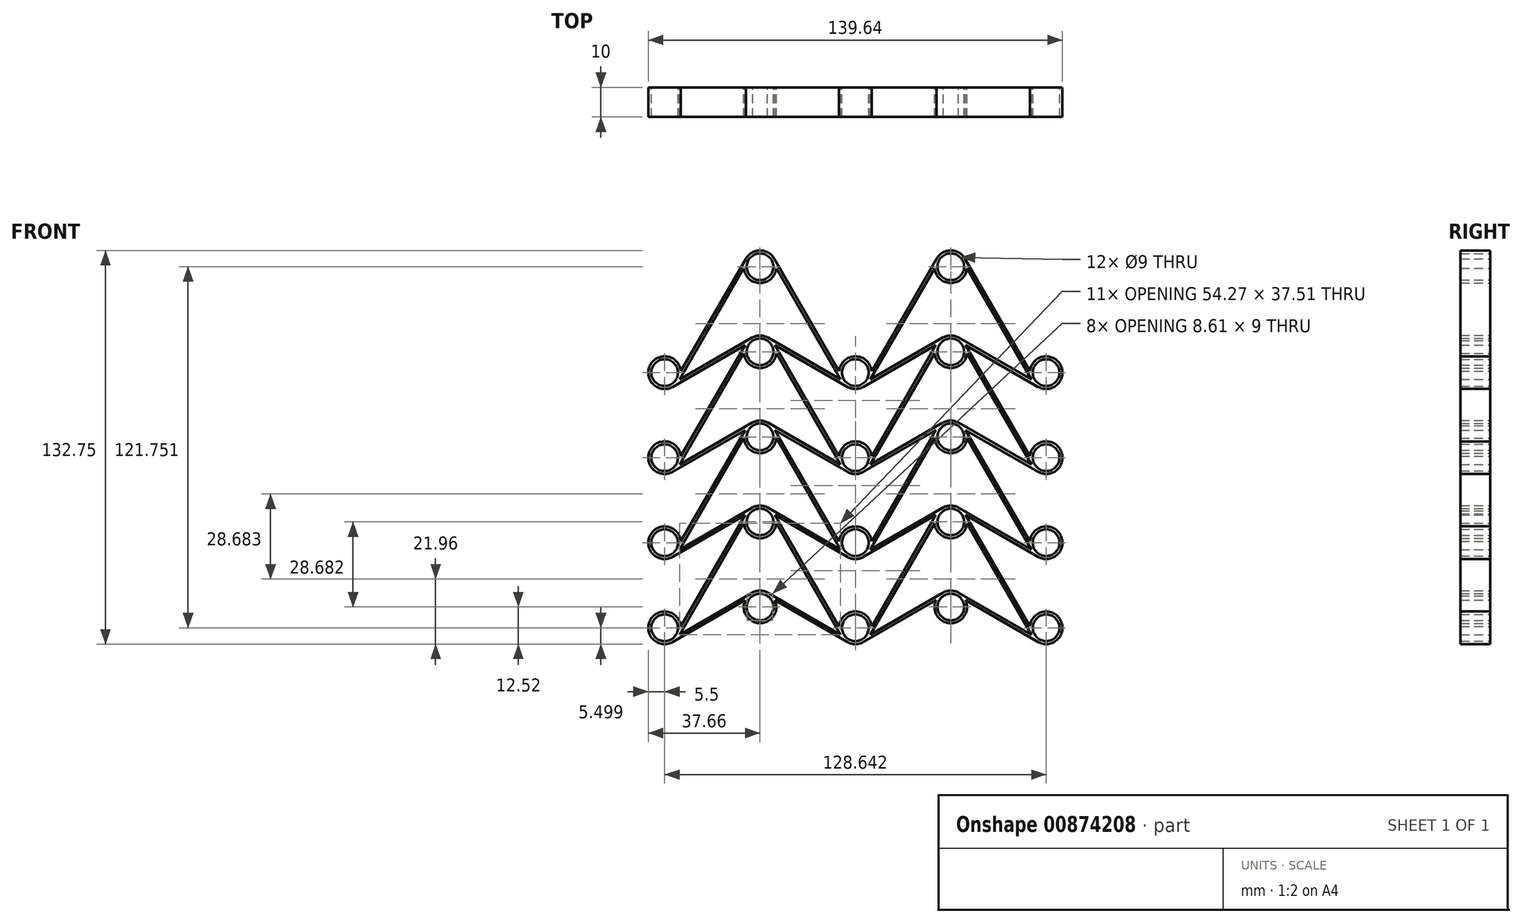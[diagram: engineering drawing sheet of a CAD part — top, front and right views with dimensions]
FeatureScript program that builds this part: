
annotation { "Feature Type Name" : "Feature", "Feature Type Description" : "" }
export const myFeature = defineFeature(function(context is Context, id is Id, definition is map)
    precondition{}
    {
        {
            var Q0;
            Q0=qCreatedBy(makeId("Front.planeOp"),FACE);
            var sketch = newSketch(context, id + "F0", { "sketchPlane" : qUnion([Q0])});
            skLineSegment(sketch, "E0", {"start": v(2.5, 3.75) * mm, "end": v(2.5, 3.74) * mm});
            skLineSegment(sketch, "E1", {"start": v(-2.5, 3.75) * mm, "end": v(-2.5, 3.74) * mm});
            skArc(sketch, "E2", {"start": v(-26.68, -6.53) * mm, "mid": v(-37.04, -4.49) * mm, "end": v(-29.41, -11.78) * mm});
            skArc(sketch, "E3", {"start": v(2.75, 33.45) * mm, "mid": v(0, 34.18) * mm, "end": v(-2.75, 33.45) * mm});
            skArc(sketch, "E4", {"start": v(-4.99, 2.32) * mm, "mid": v(0, -5.5) * mm, "end": v(4.99, 2.32) * mm});
            skCircle(sketch, "E5", {"center": v(-32.16, -7.02) * mm, "radius": 4.5 * mm});
            skCircle(sketch, "E6", {"center": v(32.16, -7.02) * mm, "radius": 4.5 * mm});
            skCircle(sketch, "E7", {"center": v(0, 28.68) * mm, "radius": 4.5 * mm});
            skCircle(sketch, "E8", {"center": v(0, 0) * mm, "radius": 4.5 * mm});
            skPoint(sketch, "E9", {"position": v(-4.75, 31.46) * mm});
            skPoint(sketch, "E10", {"position": v(-3.9, 30.93) * mm});
            skLineSegment(sketch, "E11", {"start": v(-4.75, 31.46) * mm, "end": v(-4.78, 31.4) * mm});
            skLineSegment(sketch, "E12", {"start": v(-29.63, -11.34) * mm, "end": v(-29.88, -10.9) * mm});
            skLineSegment(sketch, "E13", {"start": v(-29.88, -10.9) * mm, "end": v(-29.41, -11.78) * mm});
            skLineSegment(sketch, "E14", {"start": v(-2.26, 3.9) * mm, "end": v(-2.5, 3.75) * mm});
            skLineSegment(sketch, "E15", {"start": v(-27.17, -9.34) * mm, "end": v(-2.75, 4.76) * mm});
            skLineSegment(sketch, "E16", {"start": v(2.75, 4.76) * mm, "end": v(27.17, -9.34) * mm});
            skLineSegment(sketch, "E17", {"start": v(29.41, -11.78) * mm, "end": v(4.99, 2.32) * mm});
            skLineSegment(sketch, "E18", {"start": v(26.68, -6.53) * mm, "end": v(5.03, 30.98) * mm});
            skLineSegment(sketch, "E19", {"start": v(27.13, -9.31) * mm, "end": v(5.48, 28.2) * mm});
            skLineSegment(sketch, "E20.trimOffspring", {"start": v(-4.99, 2.32) * mm, "end": v(-29.41, -11.78) * mm});
            skLineSegment(sketch, "E21.trimOffspring", {"start": v(2.5, 3.75) * mm, "end": v(2.25, 3.9) * mm});
            skArc(sketch, "E22.trimOffspring", {"start": v(2.75, 4.76) * mm, "mid": v(0, 5.5) * mm, "end": v(-2.75, 4.76) * mm});
            skArc(sketch, "E23.trimOffspring", {"start": v(29.41, -11.78) * mm, "mid": v(32.16, -12.52) * mm, "end": v(34.91, -11.78) * mm});
            skPoint(sketch, "E24.start.orphan", {"position": v(29.88, -10.9) * mm});
            skArc(sketch, "E25.trimOffspring", {"start": v(-5.48, 28.2) * mm, "mid": v(0, 23.18) * mm, "end": v(5.48, 28.2) * mm});
            skLineSegment(sketch, "E26.trimOffspring", {"start": v(-5.48, 28.2) * mm, "end": v(-27.13, -9.31) * mm});
            skPoint(sketch, "E27.orphan", {"position": v(-4.31, 31.21) * mm});
            skPoint(sketch, "E28.end.orphan", {"position": v(-5.18, 31.71) * mm});
            skLineSegment(sketch, "E29", {"start": v(2.5, 32.44) * mm, "end": v(2.5, 32.42) * mm});
            skLineSegment(sketch, "E30", {"start": v(-2.5, 32.44) * mm, "end": v(-2.5, 32.42) * mm});
            skArc(sketch, "E31", {"start": v(-26.68, 22.15) * mm, "mid": v(-37.04, 24.2) * mm, "end": v(-29.41, 16.9) * mm});
            skArc(sketch, "E32", {"start": v(2.75, 62.13) * mm, "mid": v(0, 62.86) * mm, "end": v(-2.75, 62.13) * mm});
            skCircle(sketch, "E33", {"center": v(-32.16, 21.66) * mm, "radius": 4.5 * mm});
            skCircle(sketch, "E34", {"center": v(32.16, 21.66) * mm, "radius": 4.5 * mm});
            skCircle(sketch, "E35", {"center": v(0, 57.36) * mm, "radius": 4.5 * mm});
            skPoint(sketch, "E36", {"position": v(-4.8, 60.06) * mm});
            skPoint(sketch, "E37", {"position": v(-3.9, 59.61) * mm});
            skLineSegment(sketch, "E38", {"start": v(-5.03, 59.66) * mm, "end": v(-26.68, 22.15) * mm});
            skLineSegment(sketch, "E39", {"start": v(-29.65, 17.34) * mm, "end": v(-29.9, 17.77) * mm});
            skLineSegment(sketch, "E40", {"start": v(-29.9, 17.77) * mm, "end": v(-29.41, 16.9) * mm});
            skLineSegment(sketch, "E41", {"start": v(-2.26, 32.57) * mm, "end": v(-2.5, 32.44) * mm});
            skLineSegment(sketch, "E42", {"start": v(-27.17, 19.35) * mm, "end": v(-2.75, 33.45) * mm});
            skLineSegment(sketch, "E43", {"start": v(2.75, 33.45) * mm, "end": v(27.17, 19.35) * mm});
            skLineSegment(sketch, "E44", {"start": v(29.41, 16.9) * mm, "end": v(4.99, 31) * mm});
            skLineSegment(sketch, "E45", {"start": v(26.68, 22.15) * mm, "end": v(5.03, 59.66) * mm});
            skLineSegment(sketch, "E46", {"start": v(27.13, 19.37) * mm, "end": v(5.48, 56.88) * mm});
            skLineSegment(sketch, "E47.trimOffspring", {"start": v(-4.99, 31) * mm, "end": v(-29.41, 16.9) * mm});
            skLineSegment(sketch, "E48.trimOffspring", {"start": v(2.5, 32.44) * mm, "end": v(2.25, 32.58) * mm});
            skArc(sketch, "E49.trimOffspring", {"start": v(29.41, 16.9) * mm, "mid": v(32.16, 16.16) * mm, "end": v(34.91, 16.9) * mm});
            skPoint(sketch, "E50.start.orphan", {"position": v(29.9, 17.77) * mm});
            skArc(sketch, "E51.trimOffspring", {"start": v(-5.48, 56.88) * mm, "mid": v(0, 51.86) * mm, "end": v(5.48, 56.88) * mm});
            skLineSegment(sketch, "E52.trimOffspring", {"start": v(-5.48, 56.88) * mm, "end": v(-27.13, 19.37) * mm});
            skPoint(sketch, "E53.orphan", {"position": v(-4.36, 59.81) * mm});
            skPoint(sketch, "E54.end.orphan", {"position": v(-5.23, 60.3) * mm});
            skLineSegment(sketch, "E55", {"start": v(2.5, 61.12) * mm, "end": v(2.5, 61.1) * mm});
            skLineSegment(sketch, "E56", {"start": v(-2.5, 61.12) * mm, "end": v(-2.5, 61.1) * mm});
            skArc(sketch, "E57", {"start": v(-26.68, 50.83) * mm, "mid": v(-37.04, 52.88) * mm, "end": v(-29.41, 45.58) * mm});
            skArc(sketch, "E58", {"start": v(4.76, 88.8) * mm, "mid": v(-0.04, 91.55) * mm, "end": v(-4.8, 88.74) * mm});
            skCircle(sketch, "E59", {"center": v(-32.16, 50.34) * mm, "radius": 4.5 * mm});
            skCircle(sketch, "E60", {"center": v(32.16, 50.34) * mm, "radius": 4.5 * mm});
            skCircle(sketch, "E61", {"center": v(0, 86.05) * mm, "radius": 4.5 * mm});
            skPoint(sketch, "E62", {"position": v(-4.76, 88.8) * mm});
            skPoint(sketch, "E63", {"position": v(-3.9, 88.3) * mm});
            skLineSegment(sketch, "E64", {"start": v(-4.76, 88.8) * mm, "end": v(-26.68, 50.83) * mm});
            skLineSegment(sketch, "E65", {"start": v(-29.64, 46.02) * mm, "end": v(-29.9, 46.46) * mm});
            skLineSegment(sketch, "E66", {"start": v(-29.9, 46.46) * mm, "end": v(-29.41, 45.58) * mm});
            skLineSegment(sketch, "E67", {"start": v(-2.26, 61.26) * mm, "end": v(-2.5, 61.12) * mm});
            skLineSegment(sketch, "E68", {"start": v(-27.17, 48.03) * mm, "end": v(-2.75, 62.13) * mm});
            skLineSegment(sketch, "E69", {"start": v(2.75, 62.13) * mm, "end": v(27.17, 48.03) * mm});
            skLineSegment(sketch, "E70", {"start": v(29.41, 45.58) * mm, "end": v(5.03, 59.66) * mm});
            skLineSegment(sketch, "E71", {"start": v(26.68, 50.83) * mm, "end": v(4.76, 88.8) * mm});
            skLineSegment(sketch, "E72", {"start": v(27.13, 48.05) * mm, "end": v(5.48, 85.56) * mm});
            skLineSegment(sketch, "E73.trimOffspring", {"start": v(-5.03, 59.66) * mm, "end": v(-29.41, 45.58) * mm});
            skLineSegment(sketch, "E74.trimOffspring", {"start": v(2.5, 61.12) * mm, "end": v(2.25, 61.26) * mm});
            skArc(sketch, "E75.trimOffspring", {"start": v(29.41, 45.58) * mm, "mid": v(32.17, 44.84) * mm, "end": v(34.92, 45.59) * mm});
            skPoint(sketch, "E76.start.orphan", {"position": v(29.9, 46.46) * mm});
            skArc(sketch, "E77.trimOffspring", {"start": v(-5.48, 85.56) * mm, "mid": v(0, 80.55) * mm, "end": v(5.48, 85.56) * mm});
            skLineSegment(sketch, "E78.trimOffspring", {"start": v(-5.48, 85.56) * mm, "end": v(-27.13, 48.05) * mm});
            skPoint(sketch, "E79.orphan", {"position": v(-4.33, 88.55) * mm});
            skPoint(sketch, "E80.end.orphan", {"position": v(-5.2, 89.05) * mm});
            skLineSegment(sketch, "E81", {"start": v(2.5, 89.8) * mm, "end": v(2.5, 89.79) * mm});
            skLineSegment(sketch, "E82", {"start": v(-2.5, 89.8) * mm, "end": v(-2.5, 89.79) * mm});
            skArc(sketch, "E83", {"start": v(-26.68, 79.52) * mm, "mid": v(-37.04, 81.56) * mm, "end": v(-29.41, 74.26) * mm});
            skArc(sketch, "E84", {"start": v(4.76, 117.48) * mm, "mid": v(-0.03, 120.23) * mm, "end": v(-4.8, 117.42) * mm});
            skArc(sketch, "E85", {"start": v(-4.99, 88.36) * mm, "mid": v(0, 80.55) * mm, "end": v(4.99, 88.36) * mm});
            skCircle(sketch, "E86", {"center": v(-32.16, 79.03) * mm, "radius": 4.5 * mm});
            skCircle(sketch, "E87", {"center": v(32.16, 79.03) * mm, "radius": 4.5 * mm});
            skCircle(sketch, "E88", {"center": v(0, 114.73) * mm, "radius": 4.5 * mm});
            skPoint(sketch, "E89", {"position": v(-4.76, 117.48) * mm});
            skPoint(sketch, "E90", {"position": v(-3.9, 116.98) * mm});
            skLineSegment(sketch, "E91", {"start": v(-4.76, 117.48) * mm, "end": v(-26.68, 79.52) * mm});
            skLineSegment(sketch, "E92", {"start": v(-29.65, 74.7) * mm, "end": v(-29.9, 75.14) * mm});
            skLineSegment(sketch, "E93", {"start": v(-29.9, 75.14) * mm, "end": v(-29.41, 74.26) * mm});
            skLineSegment(sketch, "E94", {"start": v(-2.26, 89.94) * mm, "end": v(-2.5, 89.8) * mm});
            skLineSegment(sketch, "E95", {"start": v(-27.17, 76.71) * mm, "end": v(-2.75, 90.81) * mm});
            skLineSegment(sketch, "E96", {"start": v(2.75, 90.81) * mm, "end": v(27.17, 76.71) * mm});
            skLineSegment(sketch, "E97", {"start": v(29.41, 74.26) * mm, "end": v(4.99, 88.36) * mm});
            skLineSegment(sketch, "E98", {"start": v(26.68, 79.52) * mm, "end": v(4.76, 117.48) * mm});
            skLineSegment(sketch, "E99", {"start": v(27.13, 76.73) * mm, "end": v(5.48, 114.24) * mm});
            skLineSegment(sketch, "E100.trimOffspring", {"start": v(-4.99, 88.36) * mm, "end": v(-29.41, 74.26) * mm});
            skLineSegment(sketch, "E101.trimOffspring", {"start": v(2.5, 89.8) * mm, "end": v(2.25, 89.94) * mm});
            skArc(sketch, "E102.trimOffspring", {"start": v(2.75, 90.81) * mm, "mid": v(0, 91.55) * mm, "end": v(-2.75, 90.81) * mm});
            skArc(sketch, "E103.trimOffspring", {"start": v(29.41, 74.26) * mm, "mid": v(32.17, 73.53) * mm, "end": v(34.92, 74.27) * mm});
            skPoint(sketch, "E104.start.orphan", {"position": v(29.9, 75.14) * mm});
            skArc(sketch, "E105.trimOffspring", {"start": v(-5.48, 114.24) * mm, "mid": v(0, 109.23) * mm, "end": v(5.48, 114.24) * mm});
            skLineSegment(sketch, "E106.trimOffspring", {"start": v(-5.48, 114.24) * mm, "end": v(-27.13, 76.73) * mm});
            skPoint(sketch, "E107.orphan", {"position": v(-4.33, 117.23) * mm});
            skPoint(sketch, "E108.end.orphan", {"position": v(-5.2, 117.73) * mm});
            skLineSegment(sketch, "E109", {"start": v(66.82, 3.75) * mm, "end": v(66.82, 3.74) * mm});
            skLineSegment(sketch, "E110", {"start": v(61.82, 3.75) * mm, "end": v(61.82, 3.74) * mm});
            skArc(sketch, "E111", {"start": v(69.08, 31.43) * mm, "mid": v(64.27, 34.18) * mm, "end": v(59.51, 31.35) * mm});
            skArc(sketch, "E112", {"start": v(59.33, 2.32) * mm, "mid": v(64.32, -5.5) * mm, "end": v(69.3, 2.32) * mm});
            skCircle(sketch, "E113", {"center": v(96.48, -7.02) * mm, "radius": 4.5 * mm});
            skCircle(sketch, "E114", {"center": v(64.32, 28.68) * mm, "radius": 4.5 * mm});
            skCircle(sketch, "E115", {"center": v(64.32, 0) * mm, "radius": 4.5 * mm});
            skPoint(sketch, "E116", {"position": v(59.56, 31.43) * mm});
            skPoint(sketch, "E117", {"position": v(60.42, 30.93) * mm});
            skLineSegment(sketch, "E118", {"start": v(59.56, 31.43) * mm, "end": v(37.64, -6.53) * mm});
            skLineSegment(sketch, "E119", {"start": v(62.06, 3.9) * mm, "end": v(61.82, 3.75) * mm});
            skLineSegment(sketch, "E120", {"start": v(37.15, -9.34) * mm, "end": v(61.57, 4.76) * mm});
            skLineSegment(sketch, "E121", {"start": v(67.07, 4.76) * mm, "end": v(91.5, -9.34) * mm});
            skLineSegment(sketch, "E122", {"start": v(93.73, -11.78) * mm, "end": v(69.3, 2.32) * mm});
            skLineSegment(sketch, "E123", {"start": v(91, -6.53) * mm, "end": v(69.08, 31.43) * mm});
            skLineSegment(sketch, "E124", {"start": v(91.45, -9.31) * mm, "end": v(69.8, 28.2) * mm});
            skLineSegment(sketch, "E125.trimOffspring", {"start": v(59.33, 2.32) * mm, "end": v(34.91, -11.78) * mm});
            skLineSegment(sketch, "E126.trimOffspring", {"start": v(66.82, 3.75) * mm, "end": v(66.57, 3.9) * mm});
            skArc(sketch, "E127.trimOffspring", {"start": v(67.07, 4.76) * mm, "mid": v(64.32, 5.5) * mm, "end": v(61.57, 4.76) * mm});
            skArc(sketch, "E128.trimOffspring", {"start": v(93.73, -11.78) * mm, "mid": v(101.36, -4.48) * mm, "end": v(91, -6.53) * mm});
            skPoint(sketch, "E129.start.orphan", {"position": v(94.21, -10.9) * mm});
            skArc(sketch, "E130.trimOffspring", {"start": v(58.84, 28.2) * mm, "mid": v(64.32, 23.18) * mm, "end": v(69.8, 28.2) * mm});
            skLineSegment(sketch, "E131.trimOffspring", {"start": v(58.84, 28.2) * mm, "end": v(37.19, -9.31) * mm});
            skPoint(sketch, "E132.orphan", {"position": v(60, 31.18) * mm});
            skPoint(sketch, "E133.end.orphan", {"position": v(59.13, 31.68) * mm});
            skLineSegment(sketch, "E134", {"start": v(66.82, 32.44) * mm, "end": v(66.82, 32.42) * mm});
            skLineSegment(sketch, "E135", {"start": v(61.82, 32.44) * mm, "end": v(61.82, 32.42) * mm});
            skArc(sketch, "E136", {"start": v(67.07, 62.13) * mm, "mid": v(64.32, 62.87) * mm, "end": v(61.57, 62.13) * mm});
            skArc(sketch, "E137", {"start": v(59.33, 31) * mm, "mid": v(64.32, 23.18) * mm, "end": v(69.3, 31) * mm});
            skCircle(sketch, "E138", {"center": v(96.48, 21.66) * mm, "radius": 4.5 * mm});
            skCircle(sketch, "E139", {"center": v(64.32, 57.37) * mm, "radius": 4.5 * mm});
            skPoint(sketch, "E140", {"position": v(59.52, 60.05) * mm});
            skPoint(sketch, "E141", {"position": v(60.42, 59.62) * mm});
            skLineSegment(sketch, "E142", {"start": v(59.52, 60.05) * mm, "end": v(59.52, 60.05) * mm});
            skLineSegment(sketch, "E143", {"start": v(34.67, 17.34) * mm, "end": v(34.42, 17.77) * mm});
            skLineSegment(sketch, "E144", {"start": v(34.42, 17.77) * mm, "end": v(34.91, 16.9) * mm});
            skLineSegment(sketch, "E145", {"start": v(62.06, 32.57) * mm, "end": v(61.82, 32.44) * mm});
            skLineSegment(sketch, "E146", {"start": v(37.15, 19.35) * mm, "end": v(61.57, 33.45) * mm});
            skLineSegment(sketch, "E147", {"start": v(67.07, 33.45) * mm, "end": v(91.5, 19.35) * mm});
            skLineSegment(sketch, "E148", {"start": v(93.73, 16.9) * mm, "end": v(69.3, 31) * mm});
            skLineSegment(sketch, "E149", {"start": v(91, 22.15) * mm, "end": v(69.35, 59.66) * mm});
            skLineSegment(sketch, "E150", {"start": v(91.45, 19.37) * mm, "end": v(69.8, 56.88) * mm});
            skLineSegment(sketch, "E151.trimOffspring", {"start": v(59.33, 31) * mm, "end": v(34.91, 16.9) * mm});
            skLineSegment(sketch, "E152.trimOffspring", {"start": v(66.82, 32.44) * mm, "end": v(66.57, 32.58) * mm});
            skArc(sketch, "E153.trimOffspring", {"start": v(67.07, 33.45) * mm, "mid": v(64.32, 34.18) * mm, "end": v(61.57, 33.45) * mm});
            skArc(sketch, "E154.trimOffspring", {"start": v(93.73, 16.9) * mm, "mid": v(101.36, 24.2) * mm, "end": v(91, 22.15) * mm});
            skPoint(sketch, "E155.start.orphan", {"position": v(94.22, 17.77) * mm});
            skArc(sketch, "E156.trimOffspring", {"start": v(58.84, 56.88) * mm, "mid": v(64.32, 51.87) * mm, "end": v(69.8, 56.88) * mm});
            skLineSegment(sketch, "E157.trimOffspring", {"start": v(58.84, 56.88) * mm, "end": v(37.19, 19.37) * mm});
            skPoint(sketch, "E158.orphan", {"position": v(59.95, 59.8) * mm});
            skPoint(sketch, "E159.end.orphan", {"position": v(59.09, 60.3) * mm});
            skLineSegment(sketch, "E160", {"start": v(66.82, 61.12) * mm, "end": v(66.82, 61.1) * mm});
            skLineSegment(sketch, "E161", {"start": v(61.82, 61.12) * mm, "end": v(61.82, 61.1) * mm});
            skArc(sketch, "E162", {"start": v(69.08, 88.8) * mm, "mid": v(64.3, 91.55) * mm, "end": v(59.53, 88.75) * mm});
            skCircle(sketch, "E163", {"center": v(96.48, 50.34) * mm, "radius": 4.5 * mm});
            skCircle(sketch, "E164", {"center": v(64.32, 86.05) * mm, "radius": 4.5 * mm});
            skPoint(sketch, "E165", {"position": v(59.56, 88.8) * mm});
            skPoint(sketch, "E166", {"position": v(60.42, 88.3) * mm});
            skLineSegment(sketch, "E167", {"start": v(59.56, 88.8) * mm, "end": v(37.64, 50.83) * mm});
            skLineSegment(sketch, "E168", {"start": v(34.68, 46.03) * mm, "end": v(34.43, 46.46) * mm});
            skLineSegment(sketch, "E169", {"start": v(34.43, 46.46) * mm, "end": v(34.91, 45.58) * mm});
            skLineSegment(sketch, "E170", {"start": v(62.06, 61.26) * mm, "end": v(61.82, 61.12) * mm});
            skLineSegment(sketch, "E171", {"start": v(37.15, 48.03) * mm, "end": v(61.57, 62.13) * mm});
            skLineSegment(sketch, "E172", {"start": v(67.07, 62.13) * mm, "end": v(91.5, 48.03) * mm});
            skLineSegment(sketch, "E173", {"start": v(93.73, 45.58) * mm, "end": v(69.3, 59.68) * mm});
            skLineSegment(sketch, "E174", {"start": v(91, 50.83) * mm, "end": v(69.08, 88.8) * mm});
            skLineSegment(sketch, "E175", {"start": v(91.45, 48.05) * mm, "end": v(69.8, 85.56) * mm});
            skLineSegment(sketch, "E176.trimOffspring", {"start": v(59.33, 59.68) * mm, "end": v(34.91, 45.58) * mm});
            skLineSegment(sketch, "E177.trimOffspring", {"start": v(66.82, 61.12) * mm, "end": v(66.57, 61.26) * mm});
            skArc(sketch, "E178.trimOffspring", {"start": v(93.73, 45.58) * mm, "mid": v(101.36, 52.88) * mm, "end": v(91, 50.83) * mm});
            skPoint(sketch, "E179.start.orphan", {"position": v(94.21, 46.46) * mm});
            skArc(sketch, "E180.trimOffspring", {"start": v(58.84, 85.56) * mm, "mid": v(64.32, 80.55) * mm, "end": v(69.8, 85.56) * mm});
            skLineSegment(sketch, "E181.trimOffspring", {"start": v(58.84, 85.56) * mm, "end": v(37.19, 48.05) * mm});
            skPoint(sketch, "E182.orphan", {"position": v(60, 88.55) * mm});
            skPoint(sketch, "E183.end.orphan", {"position": v(59.13, 89.05) * mm});
            skLineSegment(sketch, "E184", {"start": v(66.82, 89.8) * mm, "end": v(66.82, 89.79) * mm});
            skLineSegment(sketch, "E185", {"start": v(61.82, 89.8) * mm, "end": v(61.82, 89.79) * mm});
            skArc(sketch, "E186", {"start": v(69.08, 117.48) * mm, "mid": v(64.29, 120.23) * mm, "end": v(59.53, 117.43) * mm});
            skArc(sketch, "E187", {"start": v(59.33, 88.36) * mm, "mid": v(64.32, 80.55) * mm, "end": v(69.3, 88.36) * mm});
            skCircle(sketch, "E188", {"center": v(96.48, 79.03) * mm, "radius": 4.5 * mm});
            skCircle(sketch, "E189", {"center": v(64.32, 114.73) * mm, "radius": 4.5 * mm});
            skPoint(sketch, "E190", {"position": v(59.56, 117.48) * mm});
            skPoint(sketch, "E191", {"position": v(60.42, 116.98) * mm});
            skLineSegment(sketch, "E192", {"start": v(59.56, 117.48) * mm, "end": v(37.64, 79.52) * mm});
            skLineSegment(sketch, "E193", {"start": v(34.67, 74.7) * mm, "end": v(34.42, 75.14) * mm});
            skLineSegment(sketch, "E194", {"start": v(34.42, 75.14) * mm, "end": v(34.91, 74.26) * mm});
            skLineSegment(sketch, "E195", {"start": v(62.06, 89.94) * mm, "end": v(61.82, 89.8) * mm});
            skLineSegment(sketch, "E196", {"start": v(37.15, 76.71) * mm, "end": v(61.57, 90.81) * mm});
            skLineSegment(sketch, "E197", {"start": v(67.07, 90.81) * mm, "end": v(91.5, 76.71) * mm});
            skLineSegment(sketch, "E198", {"start": v(93.73, 74.26) * mm, "end": v(69.3, 88.36) * mm});
            skLineSegment(sketch, "E199", {"start": v(91, 79.52) * mm, "end": v(69.08, 117.48) * mm});
            skLineSegment(sketch, "E200", {"start": v(91.45, 76.73) * mm, "end": v(69.8, 114.24) * mm});
            skLineSegment(sketch, "E201.trimOffspring", {"start": v(59.33, 88.36) * mm, "end": v(34.91, 74.26) * mm});
            skLineSegment(sketch, "E202.trimOffspring", {"start": v(66.82, 89.8) * mm, "end": v(66.57, 89.94) * mm});
            skArc(sketch, "E203.trimOffspring", {"start": v(67.07, 90.81) * mm, "mid": v(64.32, 91.55) * mm, "end": v(61.57, 90.81) * mm});
            skArc(sketch, "E204.trimOffspring", {"start": v(93.73, 74.26) * mm, "mid": v(101.36, 81.56) * mm, "end": v(91, 79.52) * mm});
            skPoint(sketch, "E205.start.orphan", {"position": v(94.22, 75.14) * mm});
            skArc(sketch, "E206.trimOffspring", {"start": v(58.84, 114.24) * mm, "mid": v(64.32, 109.23) * mm, "end": v(69.8, 114.24) * mm});
            skLineSegment(sketch, "E207.trimOffspring", {"start": v(58.84, 114.24) * mm, "end": v(37.19, 76.73) * mm});
            skPoint(sketch, "E208.orphan", {"position": v(60, 117.23) * mm});
            skPoint(sketch, "E209.end.orphan", {"position": v(59.13, 117.73) * mm});
            skArc(sketch, "E210.trimOffspring", {"start": v(29.38, 74.28) * mm, "mid": v(32.15, 73.53) * mm, "end": v(34.91, 74.26) * mm});
            skArc(sketch, "E211.trimOffspring", {"start": v(37.64, 79.52) * mm, "mid": v(32.16, 84.53) * mm, "end": v(26.68, 79.52) * mm});
            skArc(sketch, "E212.trimOffspring", {"start": v(29.39, 45.6) * mm, "mid": v(32.15, 44.84) * mm, "end": v(34.91, 45.58) * mm});
            skArc(sketch, "E213.trimOffspring", {"start": v(37.64, 50.83) * mm, "mid": v(32.16, 55.84) * mm, "end": v(26.68, 50.83) * mm});
            skArc(sketch, "E214.trimOffspring", {"start": v(29.38, 16.91) * mm, "mid": v(32.15, 16.16) * mm, "end": v(34.91, 16.9) * mm});
            skArc(sketch, "E215.trimOffspring", {"start": v(37.64, 22.15) * mm, "mid": v(32.16, 27.16) * mm, "end": v(26.68, 22.15) * mm});
            skArc(sketch, "E216.trimOffspring", {"start": v(29.38, -11.77) * mm, "mid": v(32.14, -12.52) * mm, "end": v(34.91, -11.78) * mm});
            skPoint(sketch, "E217.end.orphan", {"position": v(34.43, -10.9) * mm});
            skArc(sketch, "E218.trimOffspring", {"start": v(37.64, -6.53) * mm, "mid": v(32.16, -1.52) * mm, "end": v(26.68, -6.53) * mm});
            skArc(sketch, "E219.trimOffspring", {"start": v(-4.75, 31.46) * mm, "mid": v(-4.76, 31.43) * mm, "end": v(-4.78, 31.4) * mm});
            skLineSegment(sketch, "E220.trimOffspring", {"start": v(-5.03, 30.98) * mm, "end": v(-26.68, -6.53) * mm});
            skLineSegment(sketch, "E221.trimOffspring", {"start": v(-4.8, 60.06) * mm, "end": v(-4.8, 60.06) * mm});
            skLineSegment(sketch, "E222.trimOffspring", {"start": v(59.3, 59.66) * mm, "end": v(37.64, 22.15) * mm});
            skSolve(sketch);
        }
        {
            var Q0;
            Q0 = qSketchRegion(id + "F0", true);
            extrude(context, id + "F1", {"entities" : qUnion([Q0]), "depth" : 10 * mm, "offsetDistance" : 25 * mm});
        }
    });
